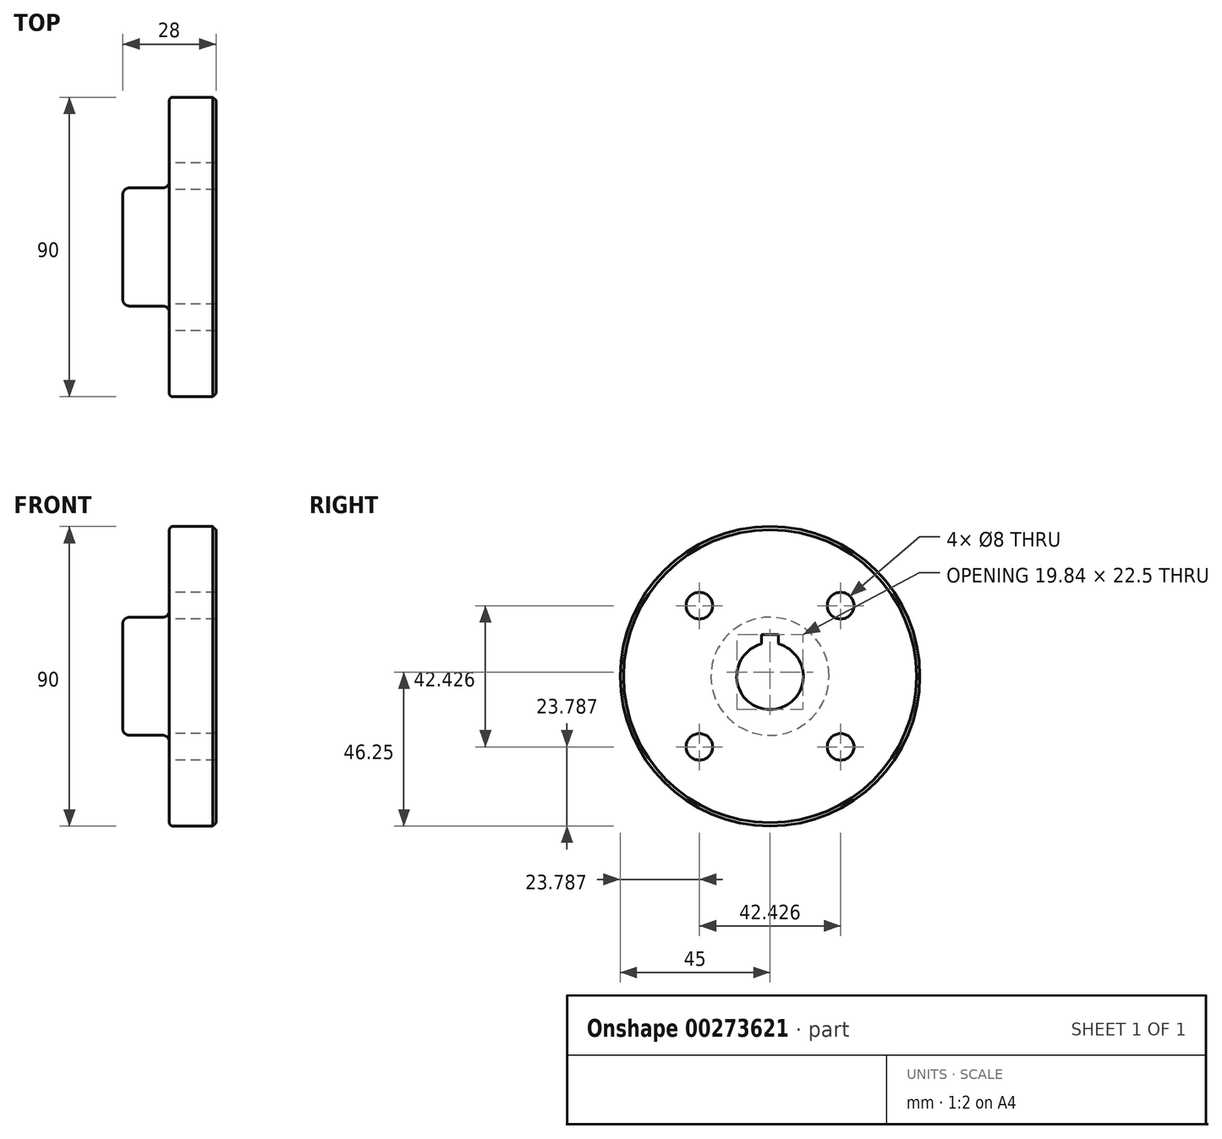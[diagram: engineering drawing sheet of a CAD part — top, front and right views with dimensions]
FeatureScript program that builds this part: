
annotation { "Feature Type Name" : "Feature", "Feature Type Description" : "" }
export const myFeature = defineFeature(function(context is Context, id is Id, definition is map)
    precondition{}
    {
        {
            var Q0;
            Q0=qCreatedBy(makeId("Front.planeOp"),FACE);
            var sketch = newSketch(context, id + "F0", { "sketchPlane" : qUnion([Q0])});
            skLineSegment(sketch, "E0", {"start": v(0, 45) * mm, "end": v(-14, 45) * mm});
            skLineSegment(sketch, "E1", {"start": v(-14, 45) * mm, "end": v(-14, 17.75) * mm});
            skLineSegment(sketch, "E2", {"start": v(-14, 17.75) * mm, "end": v(-28, 17.75) * mm});
            skLineSegment(sketch, "E3", {"start": v(-28, 17.75) * mm, "end": v(-28, 10) * mm});
            skLineSegment(sketch, "E4", {"start": v(0, 10) * mm, "end": v(0, 45) * mm});
            skLineSegment(sketch, "E5", {"start": v(-28, 10) * mm, "end": v(0, 10) * mm});
            skLineSegment(sketch, "E6", {"start": v(-49, 0) * mm, "end": v(14.81, 0) * mm, "construction": true});
            skSolve(sketch);
        }
        {
            var Q0;
            Q0=makeQuery(id+"F0.imprint","IMPRINT",FACE,{"disambiguationData":[TD([[makeQuery(id+"F0.imprint","IMPRINT",EDGE,{"derivedFrom":sQuery(id+"F0.wireOp",EDGE,"E0")}),1.0]])]});
            var Q1;
            Q1=sQuery(id+"F0.wireOp",EDGE,"E6");
            revolve(context, id + "F1", {"entities" : qUnion([Q0]), "axis" : qUnion([Q1]), "revolveType" : RevolveType.FULL});
        }
        {
            var Q0;
            Q0=makeQuery(id+"F1.opRevolve","SWEPT_FACE",FACE,{"disambiguationData":[OSD([sQuery(id+"F0.wireOp",EDGE,"E1")])]});
            var sketch = newSketch(context, id + "F2", { "sketchPlane" : qUnion([Q0])});
            skLineSegment(sketch, "E7", {"start": v(0, 0) * mm, "end": v(21.21, 21.21) * mm, "construction": true});
            skLineSegment(sketch, "E8.1.0", {"start": v(0, 0) * mm, "end": v(-21.21, 21.21) * mm, "construction": true});
            skLineSegment(sketch, "E8.2.0", {"start": v(0, 0) * mm, "end": v(-21.21, -21.21) * mm, "construction": true});
            skLineSegment(sketch, "E8.3.0", {"start": v(0, 0) * mm, "end": v(21.21, -21.21) * mm, "construction": true});
            skPoint(sketch, "E8.center", {"position": v(0, 0) * mm});
            skSolve(sketch);
        }
        {
            var Q0;
            Q0=sQuery(id+"F2.wireOp",VERTEX,"E7.end");
            var Q1;
            Q1=sQuery(id+"F2.wireOp",VERTEX,"E8.1.0.end");
            var Q2;
            Q2=sQuery(id+"F2.wireOp",VERTEX,"E8.2.0.end");
            var Q3;
            Q3=sQuery(id+"F2.wireOp",VERTEX,"E8.3.0.end");
            var Q4;
            Q4=makeQuery(id+"F1.opRevolve","SWEPT_BODY",BODY,{"disambiguationData":[OSD([sQuery(id+"F0.wireOp",EDGE,"E0"),sQuery(id+"F0.wireOp",EDGE,"E1"),sQuery(id+"F0.wireOp",EDGE,"E2"),sQuery(id+"F0.wireOp",EDGE,"E3"),sQuery(id+"F0.wireOp",EDGE,"E4"),sQuery(id+"F0.wireOp",EDGE,"E5")])]});
            hole(context, id + "F3", {"style" : HoleStyle.SIMPLE, "endStyle" : HoleEndStyle.THROUGH, "holeDiameter" : 8 * mm, "tappedDepth" : 12 * mm, "tapClearance" : 3, "locations" : qUnion([Q0, Q1, Q2, Q3]), "scope" : qUnion([Q4])});
        }
        {
            var Q0;
            Q0=makeQuery(id+"F1.opRevolve","SWEPT_FACE",FACE,{"disambiguationData":[OSD([sQuery(id+"F0.wireOp",EDGE,"E3")])]});
            var sketch = newSketch(context, id + "F4", { "sketchPlane" : qUnion([Q0])});
            skLineSegment(sketch, "E9.bottom", {"start": v(-2.5, 12.5) * mm, "end": v(2.5, 12.5) * mm});
            skLineSegment(sketch, "E9.top", {"start": v(-2.5, 8) * mm, "end": v(2.5, 8) * mm});
            skLineSegment(sketch, "E9.left", {"start": v(-2.5, 12.5) * mm, "end": v(-2.5, 8) * mm});
            skLineSegment(sketch, "E9.right", {"start": v(2.5, 12.5) * mm, "end": v(2.5, 8) * mm});
            skSolve(sketch);
        }
        {
            var Q0;
            Q0=qSketchRegion(id+"F4",true);
            extrude(context, id + "F5", {"entities" : qUnion([Q0]), "operationType" : NewBodyOperationType.REMOVE, "endBound" : BoundingType.THROUGH_ALL, "oppositeDirection" : true, "depth" : 25 * mm});
        }
        {
            var Q0;
            Q0=makeQuery(id+"F1.opRevolve","SWEPT_EDGE",EDGE,{"disambiguationData":[OSD([sQuery(id+"F0.wireOp",EDGE,"E0"),sQuery(id+"F0.wireOp",EDGE,"E4")])]});
            chamfer(context, id + "F6", {"entities" : qUnion([Q0]), "width" : 1 * mm, "tangentPropagation" : true});
        }
        {
            var Q0;
            Q0=makeQuery(id+"F1.opRevolve","SWEPT_EDGE",EDGE,{"disambiguationData":[OSD([sQuery(id+"F0.wireOp",EDGE,"E0"),sQuery(id+"F0.wireOp",EDGE,"E1")])]});
            fillet(context, id + "F7", {"entities" : qUnion([Q0]), "radius" : 1 * mm, "tangentPropagation" : true, "allowEdgeOverflow" : false});
        }
        {
            var Q0;
            Q0=makeQuery(id+"F1.opRevolve","SWEPT_EDGE",EDGE,{"disambiguationData":[OSD([sQuery(id+"F0.wireOp",EDGE,"E1"),sQuery(id+"F0.wireOp",EDGE,"E2")])]});
            var Q1;
            Q1=makeQuery(id+"F1.opRevolve","SWEPT_EDGE",EDGE,{"disambiguationData":[OSD([sQuery(id+"F0.wireOp",EDGE,"E2"),sQuery(id+"F0.wireOp",EDGE,"E3")])]});
            fillet(context, id + "F8", {"entities" : qUnion([Q0, Q1]), "radius" : 2 * mm, "tangentPropagation" : true, "allowEdgeOverflow" : false});
        }
    });
